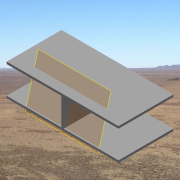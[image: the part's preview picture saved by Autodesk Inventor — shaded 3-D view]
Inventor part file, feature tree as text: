
AUTODESK INVENTOR PART (.ipt)
format: ipt  version: 2014 SP1 (Build 180222100, 222)  size: 158,720 bytes
history: native  units: in
note: dims shown in document units (in); Inventor stores cm internally (conversion verified against a paired STEP export)
features: extrude x3, plane x2, sketch x2
ambient origin geometry x8: Origin, YZ Plane, XZ Plane, XY Plane, X Axis, Y Axis, Z Axis, Center Point
bodies: Body1 (feature_tree)
feature tree (7):
  extrude  "Extrusion6"  Depth=0.12in
  plane  "Work Plane4"
  extrude  "Extrusion7"  TaperAngle=15.0deg  [1 undecoded]
  extrude  "Extrusion8"  Depth=6.12in TaperAngle=0.0deg
  plane  "Work Plane3"
  sketch  "Sketch6"  dims[d2=0.12in d17=0.12in]
  sketch  "Sketch7"  dims[d18=3.0in d19=0.0in d20=15.0deg d21=-0.5in d22=1.0in d23=0.0in d24=0.05in d25=0.05in d26=0.005in d27=0.05in d28=0.17in d29=0.0in d30=0.0in d60=2.0in d61=3.0in d62=0.12in d63=90.0deg d64=6.12in]
note: 1 required parameter value undecoded (feature->parameter linkage not recoverable at this tier; creation-order binding heuristic only, values carry confidence <= 0.55)
